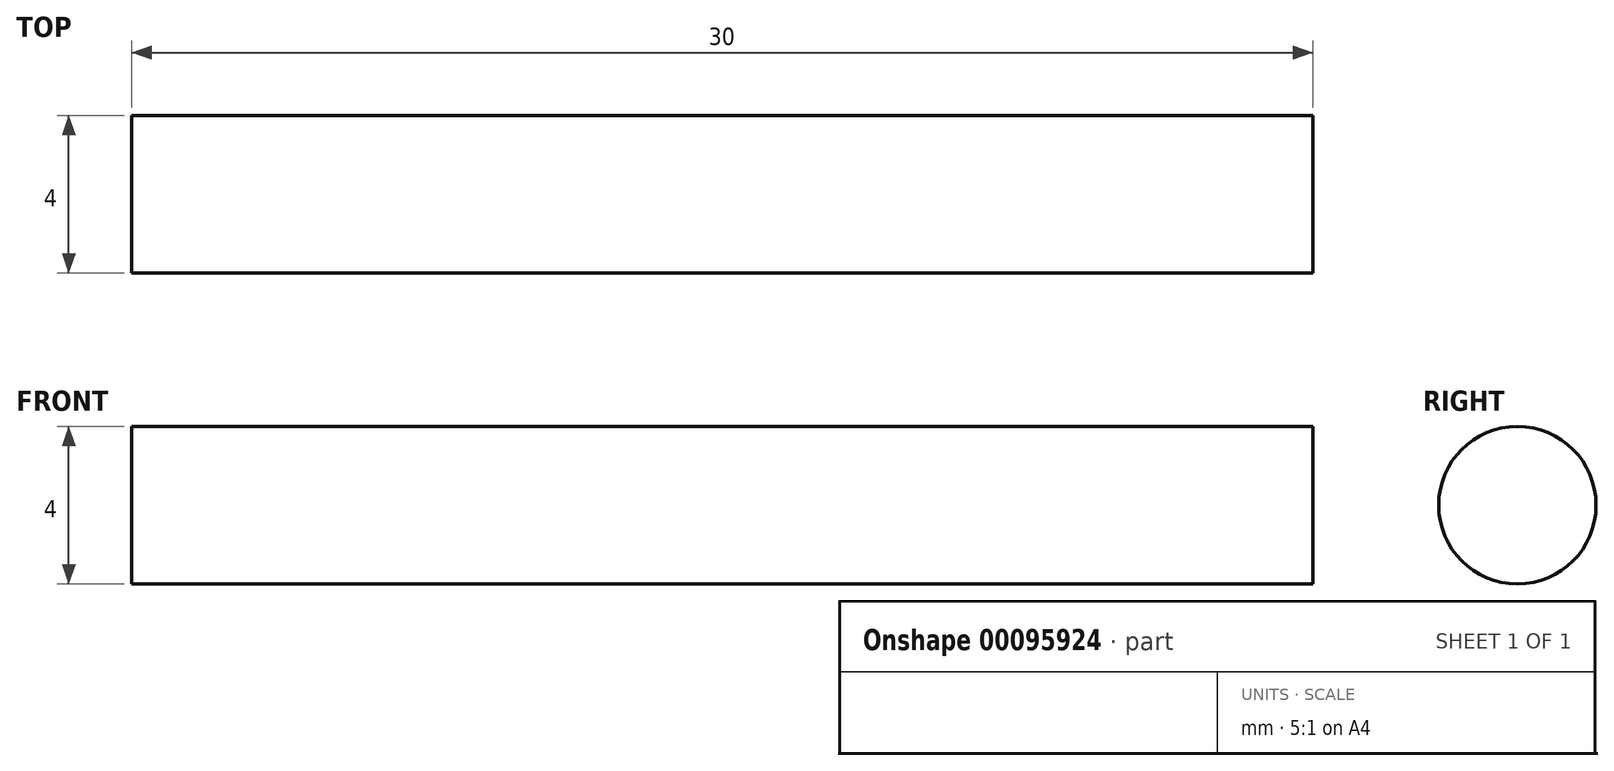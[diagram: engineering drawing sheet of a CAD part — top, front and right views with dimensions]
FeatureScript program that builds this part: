
annotation { "Feature Type Name" : "Feature", "Feature Type Description" : "" }
export const myFeature = defineFeature(function(context is Context, id is Id, definition is map)
    precondition{}
    {
        {
            var Q0;
            Q0=qCreatedBy(makeId("Right.planeOp"),FACE);
            var sketch = newSketch(context, id + "F0", { "sketchPlane" : qUnion([Q0])});
            skCircle(sketch, "E0", {"center": v(0, 0) * mm, "radius": 2 * mm});
            skSolve(sketch);
        }
        {
            var Q0;
            Q0 = qSketchRegion(id + "F0", true);
            extrude(context, id + "F1", {"entities" : qUnion([Q0]), "endBound" : BoundingType.SYMMETRIC, "depth" : 30 * mm});
        }
    });
